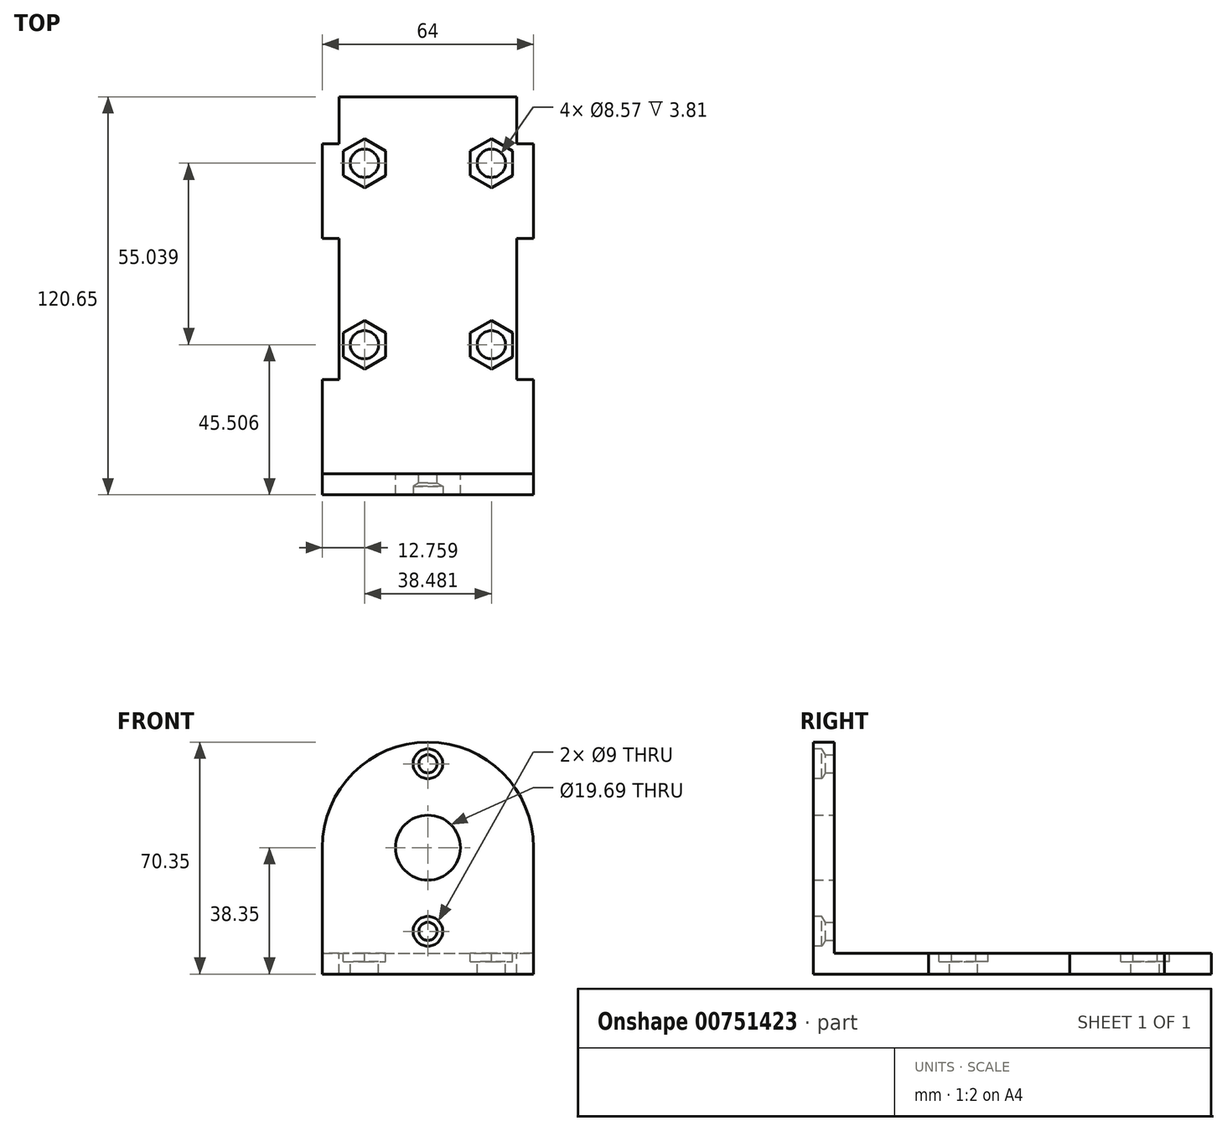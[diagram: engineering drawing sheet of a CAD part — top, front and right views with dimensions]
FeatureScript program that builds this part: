
annotation { "Feature Type Name" : "Feature", "Feature Type Description" : "" }
export const myFeature = defineFeature(function(context is Context, id is Id, definition is map)
    precondition{}
    {
        {
            var Q0;
            Q0=qCreatedBy(makeId("Front.planeOp"),FACE);
            var sketch = newSketch(context, id + "F0", { "sketchPlane" : qUnion([Q0])});
            skArc(sketch, "E0", {"start": v(32, 0) * mm, "mid": v(0, 32) * mm, "end": v(-32, 0) * mm});
            skCircle(sketch, "E1", {"center": v(0, 0) * mm, "radius": 9.84 * mm});
            skLineSegment(sketch, "E2", {"start": v(-32, 0) * mm, "end": v(-32, -32) * mm});
            skLineSegment(sketch, "E3", {"start": v(-32, -32) * mm, "end": v(32, -32) * mm});
            skLineSegment(sketch, "E4", {"start": v(32, -32) * mm, "end": v(32, 0) * mm});
            skLineSegment(sketch, "E5.top", {"start": v(-32, -38.35) * mm, "end": v(32, -38.35) * mm});
            skLineSegment(sketch, "E5.left", {"start": v(-32, -32) * mm, "end": v(-32, -38.35) * mm});
            skLineSegment(sketch, "E5.right", {"start": v(32, -32) * mm, "end": v(32, -38.35) * mm});
            skPoint(sketch, "E6", {"position": v(0, -25.4) * mm});
            skPoint(sketch, "E7", {"position": v(0, 25.4) * mm});
            skSolve(sketch);
        }
        {
            var Q0;
            Q0=makeQuery(id+"F0.imprint","IMPRINT",FACE,{"disambiguationData":[TD([[makeQuery(id+"F0.imprint","IMPRINT",EDGE,{"derivedFrom":sQuery(id+"F0.wireOp",EDGE,"E0")}),1.0]])]});
            var Q1;
            Q1=makeQuery(id+"F0.imprint","IMPRINT",FACE,{"disambiguationData":[TD([[makeQuery(id+"F0.imprint","IMPRINT",EDGE,{"derivedFrom":sQuery(id+"F0.wireOp",EDGE,"E3")}),-1.0]])]});
            extrude(context, id + "F1", {"entities" : qUnion([Q0, Q1]), "depth" : 6.35 * mm, "offsetDistance" : 25.4 * mm});
        }
        {
            var Q0;
            Q0=makeQuery(id+"F0.imprint","IMPRINT",FACE,{"disambiguationData":[TD([[makeQuery(id+"F0.imprint","IMPRINT",EDGE,{"derivedFrom":sQuery(id+"F0.wireOp",EDGE,"E3")}),-1.0]])]});
            extrude(context, id + "F2", {"entities" : qUnion([Q0]), "operationType" : NewBodyOperationType.ADD, "oppositeDirection" : true, "depth" : 114.3 * mm, "offsetDistance" : 25.4 * mm});
        }
        {
            var Q0;
            Q0=sQuery(id+"F0.wireOp",VERTEX,"E7");
            var Q1;
            Q1=sQuery(id+"F0.wireOp",VERTEX,"E6");
            var Q2;
            Q2=makeQuery(id+"F1.opExtrude","SWEPT_BODY",BODY,{"disambiguationData":[OSD([sQuery(id+"F0.wireOp",EDGE,"E0"),sQuery(id+"F0.wireOp",EDGE,"E1"),sQuery(id+"F0.wireOp",EDGE,"E2"),sQuery(id+"F0.wireOp",EDGE,"E4"),sQuery(id+"F0.wireOp",EDGE,"E5.top"),sQuery(id+"F0.wireOp",EDGE,"E5.left"),sQuery(id+"F0.wireOp",EDGE,"E5.right")])]});
            hole(context, id + "F3", {"style" : HoleStyle.SIMPLE, "endStyle" : HoleEndStyle.THROUGH, "oppositeDirection" : true, "standardTappedOrClearance" : lookupTablePath({ "standard" : "ISO", "fit" : "Normal", "size" : "M5", "type" : "Clearance" }), "standardBlindInLast" : lookupTablePath({ "fit" : "Standard", "standard" : "ISO", "size" : "M5", "type" : "Clearance" }), "holeDiameter" : 5.5 * mm, "majorDiameter" : 6.35 * mm, "isTappedThrough" : true, "tappedDepth" : 12.7 * mm, "tapClearance" : 3, "locations" : qUnion([Q0, Q1]), "scope" : qUnion([Q2])});
        }
        {
            var Q0;
            Q0=makeQuery(id+"F2.opExtrude","SWEPT_FACE",FACE,{"disambiguationData":[OSD([sQuery(id+"F0.wireOp",EDGE,"E3")])]});
            var sketch = newSketch(context, id + "F4", { "sketchPlane" : qUnion([Q0])});
            skCircle(sketch, "E8.cCircle", {"center": v(19.24, 94.2) * mm, "radius": 6.41 * mm, "construction": true});
            skLineSegment(sketch, "E8.0", {"start": v(25.65, 97.9) * mm, "end": v(25.65, 90.5) * mm});
            skLineSegment(sketch, "E8.1", {"start": v(25.65, 90.5) * mm, "end": v(19.24, 86.79) * mm});
            skLineSegment(sketch, "E8.2", {"start": v(19.24, 86.79) * mm, "end": v(12.83, 90.5) * mm});
            skLineSegment(sketch, "E8.3", {"start": v(12.83, 90.5) * mm, "end": v(12.83, 97.9) * mm});
            skLineSegment(sketch, "E8.4", {"start": v(12.83, 97.9) * mm, "end": v(19.24, 101.6) * mm});
            skLineSegment(sketch, "E8.5", {"start": v(19.24, 101.6) * mm, "end": v(25.65, 97.9) * mm});
            skPoint(sketch, "E8.0.midPoint", {"position": v(25.65, 94.2) * mm});
            skCircle(sketch, "E9", {"center": v(19.24, 94.2) * mm, "radius": 4.29 * mm});
            skCircle(sketch, "E10.cCircle", {"center": v(-19.24, 94.2) * mm, "radius": 6.41 * mm, "construction": true});
            skLineSegment(sketch, "E10.0", {"start": v(-12.83, 97.9) * mm, "end": v(-12.83, 90.5) * mm});
            skLineSegment(sketch, "E10.1", {"start": v(-12.83, 90.5) * mm, "end": v(-19.24, 86.79) * mm});
            skLineSegment(sketch, "E10.2", {"start": v(-19.24, 86.79) * mm, "end": v(-25.65, 90.5) * mm});
            skLineSegment(sketch, "E10.3", {"start": v(-25.65, 90.5) * mm, "end": v(-25.65, 97.9) * mm});
            skLineSegment(sketch, "E10.4", {"start": v(-25.65, 97.9) * mm, "end": v(-19.24, 101.6) * mm});
            skLineSegment(sketch, "E10.5", {"start": v(-19.24, 101.6) * mm, "end": v(-12.83, 97.9) * mm});
            skPoint(sketch, "E10.0.midPoint", {"position": v(-12.83, 94.2) * mm});
            skCircle(sketch, "E11", {"center": v(-19.24, 94.2) * mm, "radius": 4.29 * mm});
            skCircle(sketch, "E12.cCircle", {"center": v(-19.24, 39.16) * mm, "radius": 6.41 * mm, "construction": true});
            skLineSegment(sketch, "E12.0", {"start": v(-12.83, 42.86) * mm, "end": v(-12.83, 35.45) * mm});
            skLineSegment(sketch, "E12.1", {"start": v(-12.83, 35.45) * mm, "end": v(-19.24, 31.75) * mm});
            skLineSegment(sketch, "E12.2", {"start": v(-19.24, 31.75) * mm, "end": v(-25.65, 35.45) * mm});
            skLineSegment(sketch, "E12.3", {"start": v(-25.65, 35.45) * mm, "end": v(-25.65, 42.86) * mm});
            skLineSegment(sketch, "E12.4", {"start": v(-25.65, 42.86) * mm, "end": v(-19.24, 46.56) * mm});
            skLineSegment(sketch, "E12.5", {"start": v(-19.24, 46.56) * mm, "end": v(-12.83, 42.86) * mm});
            skPoint(sketch, "E12.0.midPoint", {"position": v(-12.83, 39.16) * mm});
            skCircle(sketch, "E13", {"center": v(-19.24, 39.16) * mm, "radius": 4.29 * mm});
            skCircle(sketch, "E14.cCircle", {"center": v(19.24, 39.16) * mm, "radius": 6.41 * mm, "construction": true});
            skLineSegment(sketch, "E14.0", {"start": v(25.65, 42.86) * mm, "end": v(25.65, 35.45) * mm});
            skLineSegment(sketch, "E14.1", {"start": v(25.65, 35.45) * mm, "end": v(19.24, 31.75) * mm});
            skLineSegment(sketch, "E14.2", {"start": v(19.24, 31.75) * mm, "end": v(12.83, 35.45) * mm});
            skLineSegment(sketch, "E14.3", {"start": v(12.83, 35.45) * mm, "end": v(12.83, 42.86) * mm});
            skLineSegment(sketch, "E14.4", {"start": v(12.83, 42.86) * mm, "end": v(19.24, 46.56) * mm});
            skLineSegment(sketch, "E14.5", {"start": v(19.24, 46.56) * mm, "end": v(25.65, 42.86) * mm});
            skPoint(sketch, "E14.0.midPoint", {"position": v(25.65, 39.16) * mm});
            skCircle(sketch, "E15", {"center": v(19.24, 39.16) * mm, "radius": 4.29 * mm});
            skLineSegment(sketch, "E16.bottom", {"start": v(26.92, 114.3) * mm, "end": v(32, 114.3) * mm});
            skLineSegment(sketch, "E16.top", {"start": v(26.92, 100.08) * mm, "end": v(32, 100.08) * mm});
            skLineSegment(sketch, "E16.left", {"start": v(26.92, 114.3) * mm, "end": v(26.92, 100.08) * mm});
            skLineSegment(sketch, "E16.right", {"start": v(32, 114.3) * mm, "end": v(32, 100.08) * mm});
            skLineSegment(sketch, "E17.bottom", {"start": v(32, 71.37) * mm, "end": v(26.92, 71.37) * mm});
            skLineSegment(sketch, "E17.top", {"start": v(32, 28.58) * mm, "end": v(26.92, 28.58) * mm});
            skLineSegment(sketch, "E17.left", {"start": v(32, 71.37) * mm, "end": v(32, 28.58) * mm});
            skLineSegment(sketch, "E17.right", {"start": v(26.92, 71.37) * mm, "end": v(26.92, 28.58) * mm});
            skLineSegment(sketch, "E18", {"start": v(0, 114.3) * mm, "end": v(0, 0) * mm, "construction": true});
            skLineSegment(sketch, "E19.MirrorCS", {"start": v(-26.92, 114.3) * mm, "end": v(-26.92, 100.08) * mm});
            skLineSegment(sketch, "E20.MirrorCS", {"start": v(-26.92, 114.3) * mm, "end": v(-32, 114.3) * mm});
            skLineSegment(sketch, "E21.MirrorCS", {"start": v(-32, 114.3) * mm, "end": v(-32, 100.08) * mm});
            skLineSegment(sketch, "E22.MirrorCS", {"start": v(-26.92, 100.08) * mm, "end": v(-32, 100.08) * mm});
            skLineSegment(sketch, "E23.MirrorCS", {"start": v(-26.92, 71.37) * mm, "end": v(-26.92, 28.58) * mm});
            skLineSegment(sketch, "E24.MirrorCS", {"start": v(-32, 71.37) * mm, "end": v(-26.92, 71.37) * mm});
            skLineSegment(sketch, "E25.MirrorCS", {"start": v(-32, 71.37) * mm, "end": v(-32, 28.58) * mm});
            skLineSegment(sketch, "E26.MirrorCS", {"start": v(-32, 28.58) * mm, "end": v(-26.92, 28.58) * mm});
            skSolve(sketch);
        }
        {
            var Q0;
            Q0=makeQuery(id+"F4.imprint","IMPRINT",FACE,{"disambiguationData":[TD([[makeQuery(id+"F4.imprint","IMPRINT",EDGE,{"derivedFrom":sQuery(id+"F4.wireOp",EDGE,"E10.0")}),-1.0]])]});
            var Q1;
            Q1=makeQuery(id+"F4.imprint","IMPRINT",FACE,{"disambiguationData":[TD([[makeQuery(id+"F4.imprint","IMPRINT",EDGE,{"derivedFrom":sQuery(id+"F4.wireOp",EDGE,"E8.0")}),-1.0]])]});
            var Q2;
            Q2=makeQuery(id+"F4.imprint","IMPRINT",FACE,{"disambiguationData":[TD([[makeQuery(id+"F4.imprint","IMPRINT",EDGE,{"derivedFrom":sQuery(id+"F4.wireOp",EDGE,"E14.0")}),-1.0]])]});
            var Q3;
            Q3=makeQuery(id+"F4.imprint","IMPRINT",FACE,{"disambiguationData":[TD([[makeQuery(id+"F4.imprint","IMPRINT",EDGE,{"derivedFrom":sQuery(id+"F4.wireOp",EDGE,"E12.0")}),-1.0]])]});
            extrude(context, id + "F5", {"entities" : qUnion([Q0, Q1, Q2, Q3]), "operationType" : NewBodyOperationType.REMOVE, "oppositeDirection" : true, "depth" : 2.54 * mm, "offsetDistance" : 25.4 * mm});
        }
        {
            var Q0;
            Q0=makeQuery(id+"F5.boolean.opBoolean","SPLIT",FACE,{"disambiguationData":[TD([makeQuery(id+"F5.opExtrude","SWEPT_FACE",FACE,{"disambiguationData":[OSD([sQuery(id+"F4.wireOp",EDGE,"E11")])]})])],"derivedFrom":makeQuery(id+"F2.opExtrude","SWEPT_FACE",FACE,{"disambiguationData":[OSD([sQuery(id+"F0.wireOp",EDGE,"E3")])]})});
            var Q1;
            Q1=makeQuery(id+"F5.boolean.opBoolean","SPLIT",FACE,{"disambiguationData":[TD([makeQuery(id+"F5.opExtrude","SWEPT_FACE",FACE,{"disambiguationData":[OSD([sQuery(id+"F4.wireOp",EDGE,"E9")])]})])],"derivedFrom":makeQuery(id+"F2.opExtrude","SWEPT_FACE",FACE,{"disambiguationData":[OSD([sQuery(id+"F0.wireOp",EDGE,"E3")])]})});
            var Q2;
            Q2=makeQuery(id+"F5.boolean.opBoolean","SPLIT",FACE,{"disambiguationData":[TD([makeQuery(id+"F5.opExtrude","SWEPT_FACE",FACE,{"disambiguationData":[OSD([sQuery(id+"F4.wireOp",EDGE,"E15")])]})])],"derivedFrom":makeQuery(id+"F2.opExtrude","SWEPT_FACE",FACE,{"disambiguationData":[OSD([sQuery(id+"F0.wireOp",EDGE,"E3")])]})});
            var Q3;
            Q3=makeQuery(id+"F5.boolean.opBoolean","SPLIT",FACE,{"disambiguationData":[TD([makeQuery(id+"F5.opExtrude","SWEPT_FACE",FACE,{"disambiguationData":[OSD([sQuery(id+"F4.wireOp",EDGE,"E13")])]})])],"derivedFrom":makeQuery(id+"F2.opExtrude","SWEPT_FACE",FACE,{"disambiguationData":[OSD([sQuery(id+"F0.wireOp",EDGE,"E3")])]})});
            extrude(context, id + "F6", {"entities" : qUnion([Q0, Q1, Q2, Q3]), "operationType" : NewBodyOperationType.REMOVE, "endBound" : BoundingType.THROUGH_ALL, "oppositeDirection" : true, "depth" : 25.4 * mm, "offsetDistance" : 25.4 * mm});
        }
        {
            var Q0;
            Q0=makeQuery(id+"F4.imprint","IMPRINT",FACE,{"disambiguationData":[TD([[makeQuery(id+"F4.imprint","IMPRINT",EDGE,{"derivedFrom":sQuery(id+"F4.wireOp",EDGE,"E16.bottom")}),-1.0]])]});
            var Q1;
            Q1=makeQuery(id+"F4.imprint","IMPRINT",FACE,{"disambiguationData":[TD([[makeQuery(id+"F4.imprint","IMPRINT",EDGE,{"derivedFrom":sQuery(id+"F4.wireOp",EDGE,"E17.bottom")}),1.0]])]});
            var Q2;
            Q2=makeQuery(id+"F4.imprint","IMPRINT",FACE,{"disambiguationData":[TD([[makeQuery(id+"F4.imprint","IMPRINT",EDGE,{"derivedFrom":sQuery(id+"F4.wireOp",EDGE,"E19.MirrorCS")}),-1.0]])]});
            var Q3;
            Q3=makeQuery(id+"F4.imprint","IMPRINT",FACE,{"disambiguationData":[TD([[makeQuery(id+"F4.imprint","IMPRINT",EDGE,{"derivedFrom":sQuery(id+"F4.wireOp",EDGE,"E23.MirrorCS")}),-1.0]])]});
            extrude(context, id + "F7", {"entities" : qUnion([Q0, Q1, Q2, Q3]), "operationType" : NewBodyOperationType.REMOVE, "endBound" : BoundingType.THROUGH_ALL, "oppositeDirection" : true, "depth" : 25.4 * mm, "offsetDistance" : 25.4 * mm});
        }
        {
            var Q0;
            Q0=makeQuery(id+"F1.opExtrude","CAP_FACE",FACE,{"disambiguationData":[OSD([sQuery(id+"F0.wireOp",EDGE,"E0"),sQuery(id+"F0.wireOp",EDGE,"E1"),sQuery(id+"F0.wireOp",EDGE,"E2"),sQuery(id+"F0.wireOp",EDGE,"E4"),sQuery(id+"F0.wireOp",EDGE,"E5.top"),sQuery(id+"F0.wireOp",EDGE,"E5.left"),sQuery(id+"F0.wireOp",EDGE,"E5.right")])],"isStart":false});
            var sketch = newSketch(context, id + "F8", { "sketchPlane" : qUnion([Q0])});
            skPoint(sketch, "E27", {"position": v(0, 25.4) * mm});
            skPoint(sketch, "E28", {"position": v(0, -25.4) * mm});
            skSolve(sketch);
        }
        {
            var Q0;
            Q0=sQuery(id+"F8.wireOp",VERTEX,"E27");
            var Q1;
            Q1=sQuery(id+"F8.wireOp",VERTEX,"E28");
            var Q2;
            Q2=makeQuery(id+"F1.opExtrude","SWEPT_BODY",BODY,{"disambiguationData":[OSD([sQuery(id+"F0.wireOp",EDGE,"E0"),sQuery(id+"F0.wireOp",EDGE,"E1"),sQuery(id+"F0.wireOp",EDGE,"E2"),sQuery(id+"F0.wireOp",EDGE,"E4"),sQuery(id+"F0.wireOp",EDGE,"E5.top"),sQuery(id+"F0.wireOp",EDGE,"E5.left"),sQuery(id+"F0.wireOp",EDGE,"E5.right")])]});
            hole(context, id + "F9", {"style" : HoleStyle.SIMPLE, "endStyle" : HoleEndStyle.BLIND, "holeDiameter" : 9 * mm, "majorDiameter" : 6.35 * mm, "holeDepth" : 2.54 * mm, "isTappedThrough" : true, "tappedDepth" : 12.7 * mm, "tapClearance" : 3, "locations" : qUnion([Q0, Q1]), "scope" : qUnion([Q2])});
        }
    });
